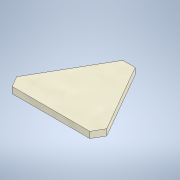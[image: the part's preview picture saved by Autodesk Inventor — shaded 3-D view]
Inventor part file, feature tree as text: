
AUTODESK INVENTOR PART (.ipt)
format: ipt  version: 2021 (Build 250183000, 183)  size: 106,496 bytes
history: native  units: mm
features: extrude x1, sketch x1
ambient origin geometry x8: Origin, YZ Plane, XZ Plane, XY Plane, X Axis, Y Axis, Z Axis, Center Point
bodies: Solid1 (feature_tree)
feature tree (2):
  extrude  "Extrusion1"  Depth=1.75mm
  sketch  "Sketch1"  dims[d0=21.8mm d1=3.464102mm d2=1.75mm d3=0.0mm d4=24.8mm]
